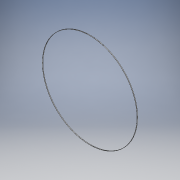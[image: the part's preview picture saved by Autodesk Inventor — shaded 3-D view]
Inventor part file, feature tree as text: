
AUTODESK INVENTOR PART (.ipt)
format: ipt  version: 2019 (Build 230136000, 136)  size: 104,960 bytes
history: native  units: mm
features: extrude x2, sketch x2
ambient origin geometry x8: Origin, YZ Plane, XZ Plane, XY Plane, X Axis, Y Axis, Z Axis, Center Point
bodies: Solid1 (feature_tree)
feature tree (4):
  extrude  "Extrusion1"  Depth=0.27mm TaperAngle=0.0deg
  extrude  "Extrusion2"  Depth=0.27mm TaperAngle=0.0deg
  sketch  "Sketch1"  dims[d0=41.534mm d1=0.27mm d2=0.0mm]
  sketch  "Sketch2"  dims[d3=41.4mm d4=0.27mm d5=0.0mm]
